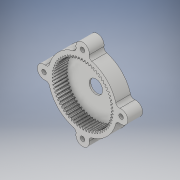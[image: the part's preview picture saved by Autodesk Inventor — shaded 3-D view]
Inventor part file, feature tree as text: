
AUTODESK INVENTOR PART (.ipt)
format: ipt  version: 2019 (Build 230136000, 136)  size: 2,307,584 bytes
history: native  units: in
note: dims shown in document units (in); Inventor stores cm internally (conversion verified against a paired STEP export)
features: sketch x9, extrude x8, projected_geometry x5, plane x2, fillet x1
ambient origin geometry x8: Origin, YZ Plane, XZ Plane, XY Plane, X Axis, Y Axis, Z Axis, Center Point
bodies: Solid1 (feature_tree)
feature tree (25):
  plane  "Work Plane2"
  plane  "Work Plane1"
  extrude  "Extrusion2"  Depth=2.2548in
  extrude  "Extrusion3"  Depth=0.19in TaperAngle=0.0deg
  extrude  "Extrusion4"  Depth=0.05in TaperAngle=0.0deg
  extrude  "Extrusion5"  Depth=0.05in TaperAngle=0.0deg
  extrude  "Extrusion6"  Depth=0.45in TaperAngle=0.0deg
  extrude  "Extrusion7"  Depth=0.15in
  extrude  "Extrusion8"  Depth=0.7874in TaperAngle=0.0deg
  extrude  "Extrusion9"  Depth=1.5748in TaperAngle=0.0deg
  sketch  "Sketch10"  dims[d37=0.4in d38=0.0in d39=0.125in]
  fillet  "Fillet1"  [1 undecoded]
  sketch  "Sketch2"  dims[d3=0.19in d4=0.0in d5=2.2548in]
  projected_geometry  "Projected Loop2"
  sketch  "Sketch3"  dims[d7=0.2in d8=0.19in d9=0.0in]
  sketch  "Sketch4"  dims[d10=0.01in d11=0.0in d12=0.05in d13=0.0in]
  projected_geometry  "Projected Loop3"
  sketch  "Sketch5"  dims[d14=0.05in d15=0.0in d16=0.2in d17=0.0in]
  projected_geometry  "Projected Loop4"
  sketch  "Sketch6"  dims[d18=0.45in d19=0.2in d20=0.0in]
  sketch  "Sketch7"  dims[d21=0.15in d22=0.15in]
  projected_geometry  "Projected Loop5"
  sketch  "Sketch8"  dims[d23=1.3in d24=0.7874in d26=0.0in]
  sketch  "Sketch9"  dims[d28=1.5748in d30=0.0in d32=1.5748in d34=0.0in d36=45.0deg]
  projected_geometry  "Projected Loop6"
note: 1 required parameter value undecoded (feature->parameter linkage not recoverable at this tier; creation-order binding heuristic only, values carry confidence <= 0.55)
